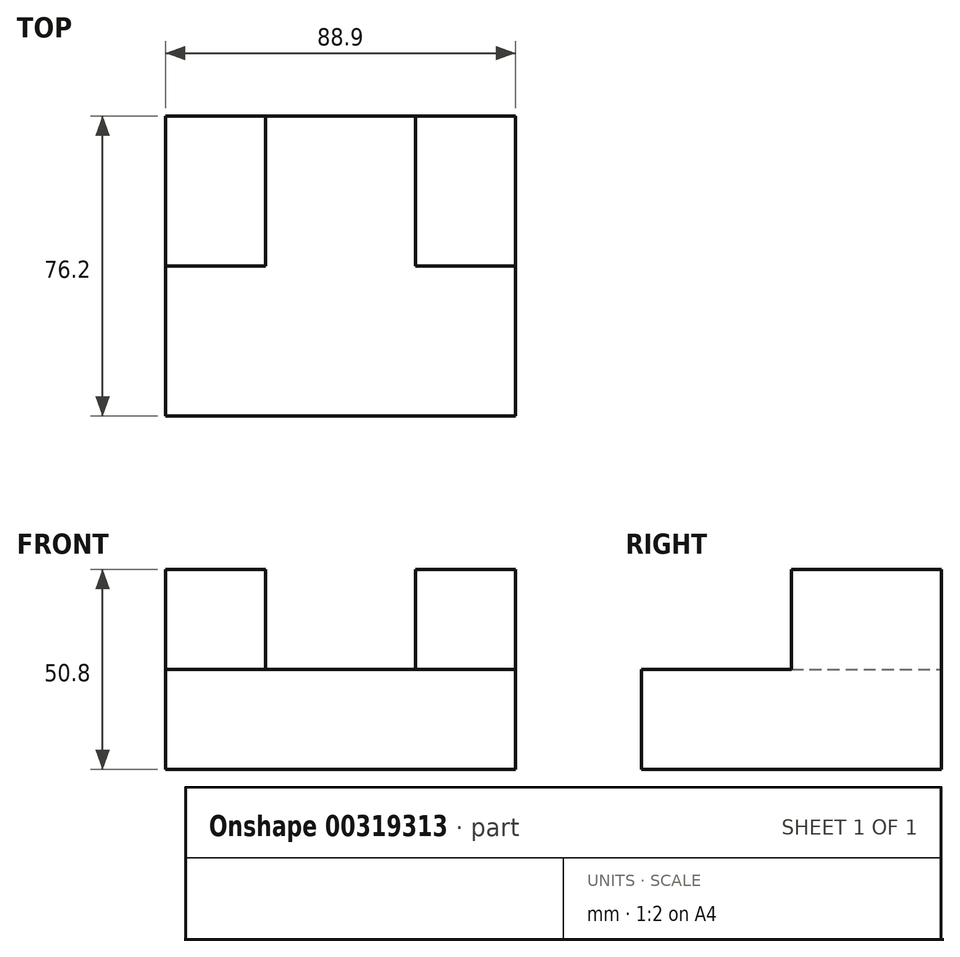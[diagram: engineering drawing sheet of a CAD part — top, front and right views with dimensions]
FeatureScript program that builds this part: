
annotation { "Feature Type Name" : "Feature", "Feature Type Description" : "" }
export const myFeature = defineFeature(function(context is Context, id is Id, definition is map)
    precondition{}
    {
        {
            var Q0;
            Q0=qCreatedBy(makeId("Top.planeOp"),FACE);
            var sketch = newSketch(context, id + "F0", { "sketchPlane" : qUnion([Q0])});
            skLineSegment(sketch, "E0", {"start": v(-48.32, -25.79) * mm, "end": v(40.58, -25.79) * mm});
            skLineSegment(sketch, "E1", {"start": v(40.58, -25.79) * mm, "end": v(40.58, 50.41) * mm});
            skLineSegment(sketch, "E2", {"start": v(40.58, 50.41) * mm, "end": v(-48.32, 50.41) * mm});
            skLineSegment(sketch, "E3", {"start": v(-48.32, 50.41) * mm, "end": v(-48.32, -25.79) * mm});
            skSolve(sketch);
        }
        {
            var Q0;
            Q0=makeQuery(id+"F0.imprint","IMPRINT",FACE,{"disambiguationData":[TD([[makeQuery(id+"F0.imprint","IMPRINT",EDGE,{"derivedFrom":sQuery(id+"F0.wireOp",EDGE,"E0")}),1.0]])]});
            extrude(context, id + "F1", {"entities" : qUnion([Q0]), "depth" : 25.4 * mm});
        }
        {
            var Q0;
            Q0=makeQuery(id+"F1.opExtrude","CAP_FACE",FACE,{"disambiguationData":[OSD([sQuery(id+"F0.wireOp",EDGE,"E0"),sQuery(id+"F0.wireOp",EDGE,"E1"),sQuery(id+"F0.wireOp",EDGE,"E2"),sQuery(id+"F0.wireOp",EDGE,"E3")])],"isStart":false});
            var sketch = newSketch(context, id + "F2", { "sketchPlane" : qUnion([Q0])});
            skLineSegment(sketch, "E4", {"start": v(-48.32, 50.41) * mm, "end": v(-48.32, 12.31) * mm});
            skLineSegment(sketch, "E5", {"start": v(-48.32, 12.31) * mm, "end": v(-22.92, 12.31) * mm});
            skLineSegment(sketch, "E6", {"start": v(-22.92, 12.31) * mm, "end": v(-22.92, 50.41) * mm});
            skLineSegment(sketch, "E7", {"start": v(-22.92, 50.41) * mm, "end": v(-48.32, 50.41) * mm});
            skSolve(sketch);
        }
        {
            var Q0;
            Q0=makeQuery(id+"F2.imprint","IMPRINT",FACE,{"disambiguationData":[TD([[makeQuery(id+"F2.imprint","IMPRINT",EDGE,{"derivedFrom":sQuery(id+"F2.wireOp",EDGE,"E4")}),1.0]])]});
            extrude(context, id + "F3", {"entities" : qUnion([Q0]), "operationType" : NewBodyOperationType.ADD, "depth" : 25.4 * mm});
        }
        {
            var Q0;
            Q0=makeQuery(id+"F1.opExtrude","CAP_FACE",FACE,{"disambiguationData":[OSD([sQuery(id+"F0.wireOp",EDGE,"E0"),sQuery(id+"F0.wireOp",EDGE,"E1"),sQuery(id+"F0.wireOp",EDGE,"E2"),sQuery(id+"F0.wireOp",EDGE,"E3")])],"isStart":false});
            var sketch = newSketch(context, id + "F4", { "sketchPlane" : qUnion([Q0])});
            skLineSegment(sketch, "E8", {"start": v(40.58, 50.41) * mm, "end": v(40.58, 12.31) * mm});
            skLineSegment(sketch, "E9", {"start": v(40.58, 12.31) * mm, "end": v(15.18, 12.31) * mm});
            skLineSegment(sketch, "E10", {"start": v(15.18, 12.31) * mm, "end": v(15.18, 50.41) * mm});
            skLineSegment(sketch, "E11", {"start": v(15.18, 50.41) * mm, "end": v(40.58, 50.41) * mm});
            skSolve(sketch);
        }
        {
            var Q0;
            Q0=makeQuery(id+"F4.imprint","IMPRINT",FACE,{"disambiguationData":[TD([[makeQuery(id+"F4.imprint","IMPRINT",EDGE,{"derivedFrom":sQuery(id+"F4.wireOp",EDGE,"E8")}),1.0]])]});
            extrude(context, id + "F5", {"entities" : qUnion([Q0]), "operationType" : NewBodyOperationType.ADD, "depth" : 25.4 * mm});
        }
    });
